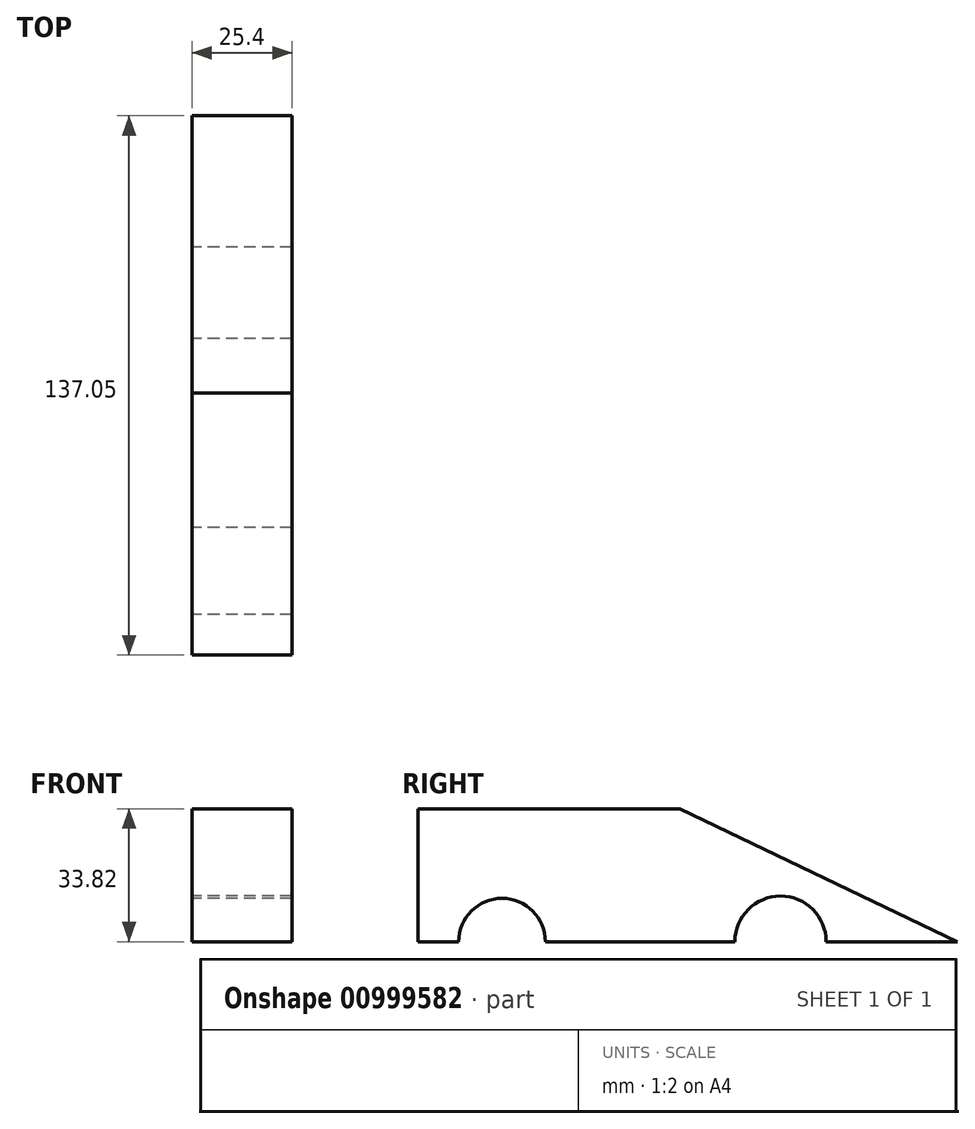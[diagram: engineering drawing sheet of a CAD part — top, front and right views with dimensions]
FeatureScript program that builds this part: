
annotation { "Feature Type Name" : "Feature", "Feature Type Description" : "" }
export const myFeature = defineFeature(function(context is Context, id is Id, definition is map)
    precondition{}
    {
        {
            var Q0;
            Q0=qCreatedBy(makeId("Right.planeOp"),FACE);
            var sketch = newSketch(context, id + "F0", { "sketchPlane" : qUnion([Q0])});
            skLineSegment(sketch, "E0", {"start": v(-66.57, 11.63) * mm, "end": v(-66.57, -22.19) * mm});
            skLineSegment(sketch, "E1", {"start": v(-66.57, -22.19) * mm, "end": v(70.48, -22.19) * mm});
            skLineSegment(sketch, "E2", {"start": v(-66.57, 11.63) * mm, "end": v(0, 11.63) * mm});
            skLineSegment(sketch, "E3", {"start": v(0, 11.63) * mm, "end": v(70.48, -22.19) * mm});
            skCircle(sketch, "E4", {"center": v(-45.2, -22.19) * mm, "radius": 11.02 * mm});
            skCircle(sketch, "E5", {"center": v(25.54, -22.19) * mm, "radius": 11.6 * mm});
            skSolve(sketch);
        }
        {
            var Q0;
            {var subQ5=sQuery(id+"F0.wireOp",EDGE,"E0");Q0=makeQuery(id+"F0.imprint","IMPRINT",FACE,{"disambiguationData":[TD([[makeQuery(id+"F0.imprint","IMPRINT",EDGE,{"derivedFrom":subQ5}),1.0]])]});}
            extrude(context, id + "F1", {"entities" : qUnion([Q0]), "depth" : 25.4 * mm, "offsetDistance" : 25.4 * mm});
        }
    });
